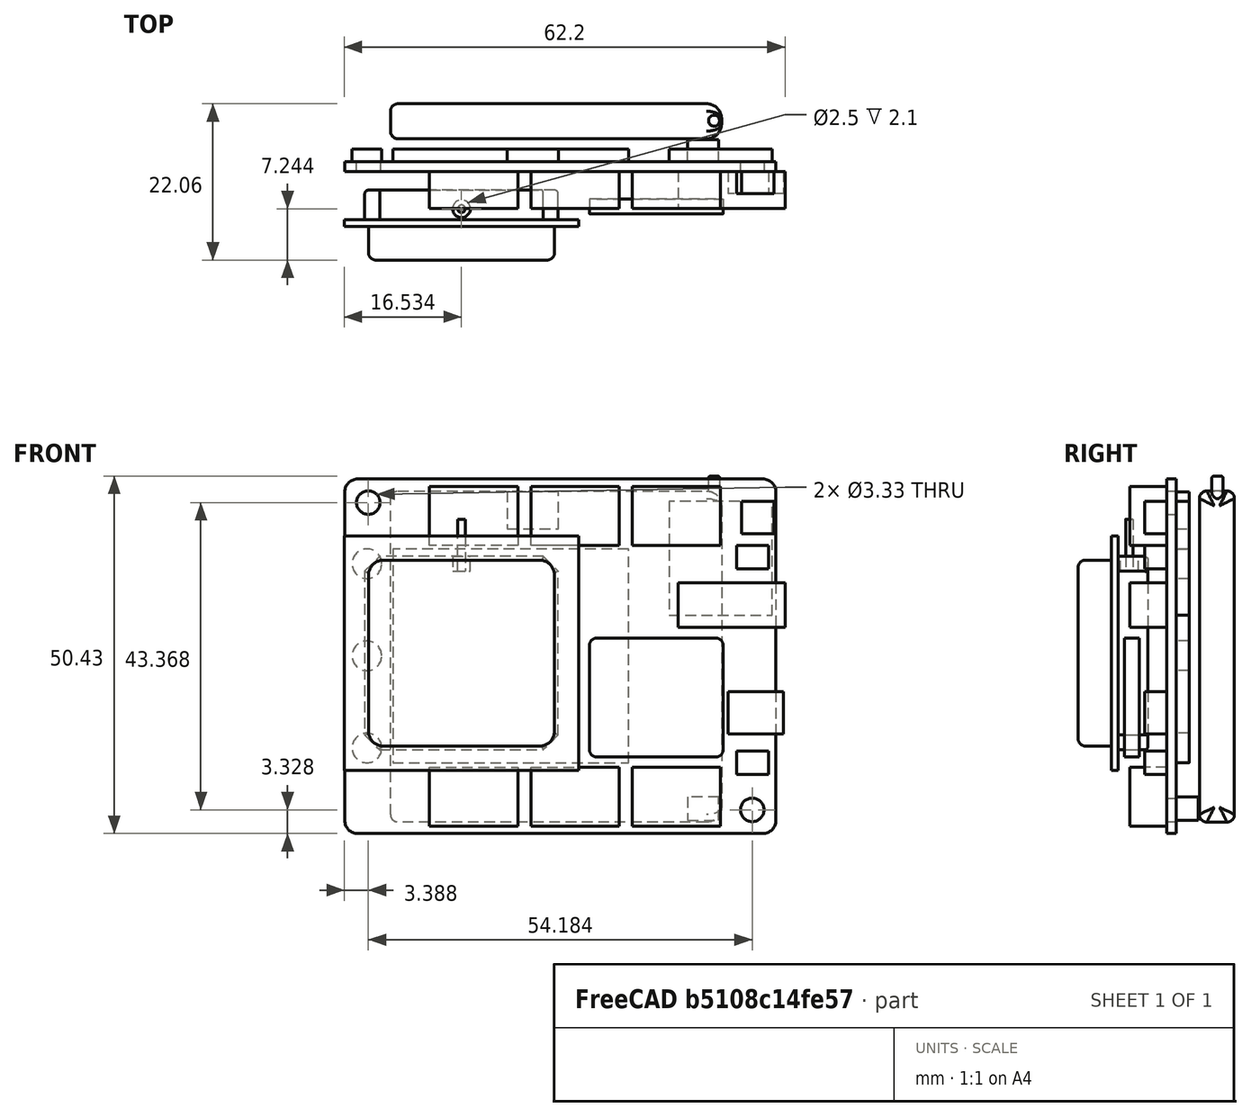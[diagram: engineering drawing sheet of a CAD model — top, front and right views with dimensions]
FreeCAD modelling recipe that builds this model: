
FCSTD DOCUMENT  (FreeCAD 0.18.1R)
Label: assemply-upscale
License: All rights reserved
LicenseURL: http://en.wikipedia.org/wiki/All_rights_reserved
objects: Part::Feature×4, Part::FeaturePython×4
note: 8 computed .brp shape members not serialized (recipe doc carries the construction recipe); baked Part::Feature solids carry a one-line shape summary decoded from their .brp

FEATURE [Part::Feature] Part__Feature  label="Wio-LTE-board_001"
  shape: bbox 59.75 x 9.3 x 48.1 mm, 95 faces (baked)
FEATURE [Part::Feature] Part__Feature001  label="GPS-a_001"
  shape: bbox 31.5 x 9.4 x 33.75 mm, 44 faces (baked)
FEATURE [Part::Feature] Part__Feature002  label="acc-gyro_001"
  shape: bbox 18 x 2 x 16 mm, 10 faces (baked)
FEATURE [Part::Feature] Part__Feature003  label="li-battery_001"
  shape: bbox 44.5 x 4.7 x 46.5 mm, 30 faces (baked)
FEATURE [Part::FeaturePython] Clone  label="Wio-LTE-board_002"  # Draft clone (typed FeaturePython)
  AttacherType = Attacher::AttachEngine3D
  Fuse = false
  Objects = -> [Part__Feature]
  Scale = (1.04,1.04,1.04)
FEATURE [Part::FeaturePython] Clone001  label="GPS-a_002"  # Draft clone (typed FeaturePython)
  AttacherType = Attacher::AttachEngine3D
  Fuse = false
  Objects = -> [Part__Feature001]
  Scale = (1.05,1.05,1.05)
FEATURE [Part::FeaturePython] Clone002  label="acc-gyro_002"  # Draft clone (typed FeaturePython)
  AttacherType = Attacher::AttachEngine3D
  Fuse = false
  Objects = -> [Part__Feature002]
  Scale = (1.05,1.05,1.05)
FEATURE [Part::FeaturePython] Clone003  label="li-battery_002"  # Draft clone (typed FeaturePython)
  AttacherType = Attacher::AttachEngine3D
  Fuse = false
  Objects = -> [Part__Feature003]
  Scale = (1.05,1.05,1.05)
